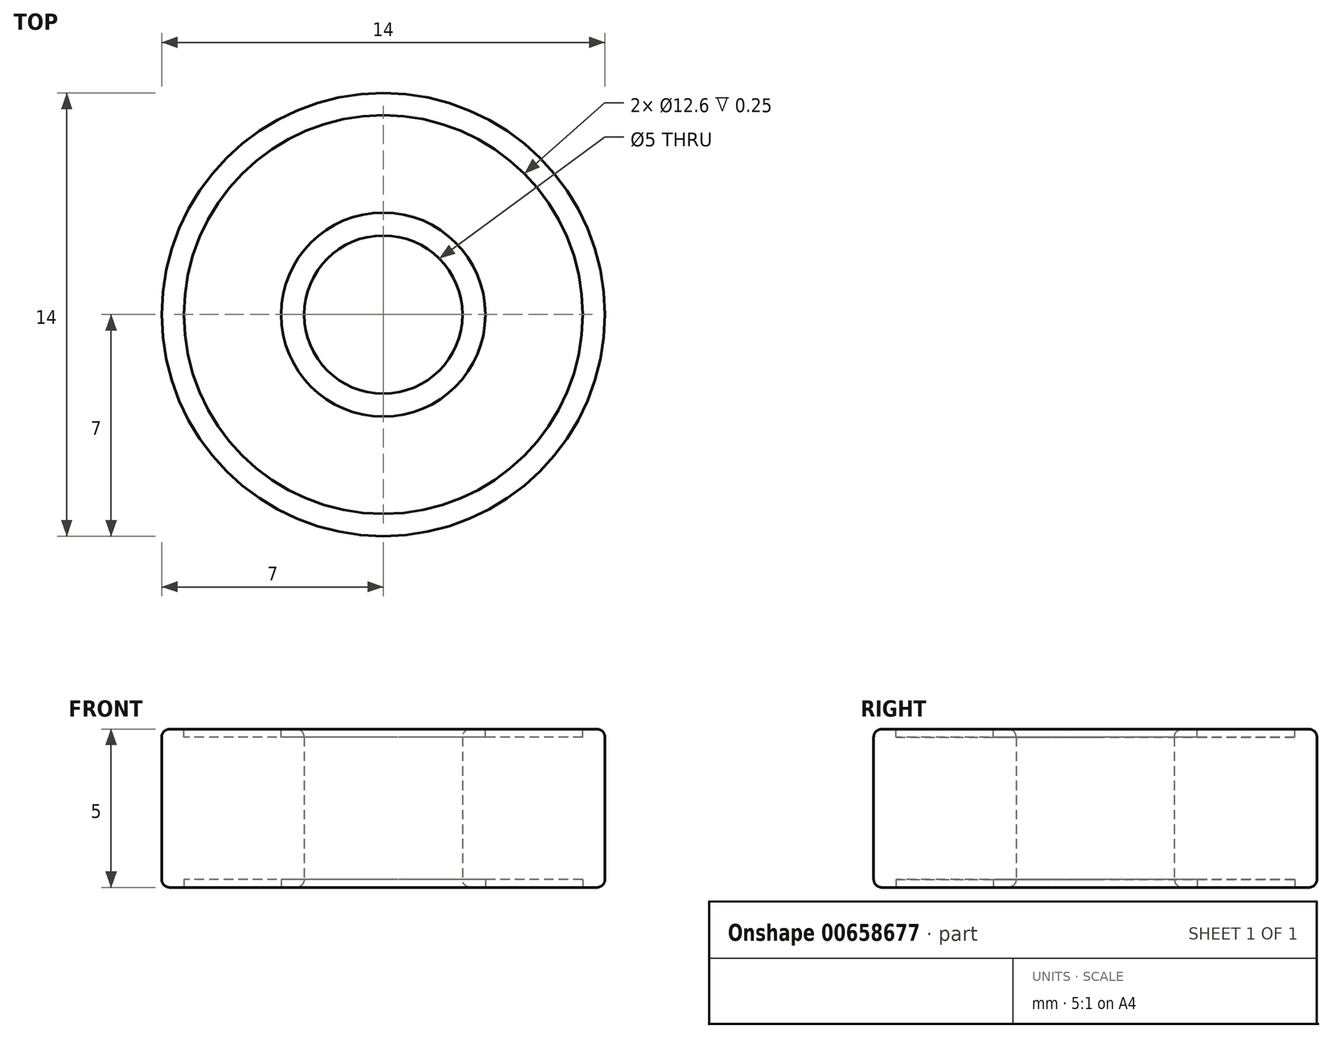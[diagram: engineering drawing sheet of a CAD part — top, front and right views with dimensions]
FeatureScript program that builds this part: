
annotation { "Feature Type Name" : "Feature", "Feature Type Description" : "" }
export const myFeature = defineFeature(function(context is Context, id is Id, definition is map)
    precondition{}
    {
        {
            var Q0;
            Q0=qCreatedBy(makeId("Top.planeOp"),FACE);
            var sketch = newSketch(context, id + "F0", { "sketchPlane" : qUnion([Q0])});
            skCircle(sketch, "E0", {"center": v(0, 0) * mm, "radius": 7 * mm});
            skCircle(sketch, "E1", {"center": v(0, 0) * mm, "radius": 2.5 * mm});
            skSolve(sketch);
        }
        {
            var Q0;
            Q0=makeQuery(id+"F0.imprint","IMPRINT",FACE,{"disambiguationData":[TD([[makeQuery(id+"F0.imprint","IMPRINT",EDGE,{"derivedFrom":sQuery(id+"F0.wireOp",EDGE,"E0")}),1.0]])]});
            extrude(context, id + "F1", {"entities" : qUnion([Q0]), "depth" : 2.5 * mm});
        }
        {
            var Q0;
            Q0=makeQuery(id+"F1.opExtrude","CAP_FACE",FACE,{"disambiguationData":[OSD([sQuery(id+"F0.wireOp",EDGE,"E0"),sQuery(id+"F0.wireOp",EDGE,"E1")])],"isStart":false});
            var sketch = newSketch(context, id + "F2", { "sketchPlane" : qUnion([Q0])});
            skCircle(sketch, "E2", {"center": v(0, 0) * mm, "radius": 3.22 * mm});
            skCircle(sketch, "E3", {"center": v(0, 0) * mm, "radius": 6.3 * mm});
            skSolve(sketch);
        }
        {
            var Q0;
            Q0=makeQuery(id+"F2.imprint","IMPRINT",FACE,{"disambiguationData":[TD([[makeQuery(id+"F2.imprint","IMPRINT",EDGE,{"derivedFrom":sQuery(id+"F2.wireOp",EDGE,"E2")}),-1.0]])]});
            extrude(context, id + "F3", {"entities" : qUnion([Q0]), "operationType" : NewBodyOperationType.REMOVE, "oppositeDirection" : true, "depth" : .25 * mm});
        }
        {
            var Q0;
            Q0=makeQuery(id+"F1.opExtrude","CAP_EDGE",EDGE,{"disambiguationData":[OSD([sQuery(id+"F0.wireOp",EDGE,"E0")])],"isStart":false});
            var Q1;
            Q1=makeQuery(id+"F1.opExtrude","CAP_EDGE",EDGE,{"disambiguationData":[OSD([sQuery(id+"F0.wireOp",EDGE,"E1")])],"isStart":false});
            fillet(context, id + "F4", {"entities" : qUnion([Q0, Q1]), "radius" : .25 * mm, "tangentPropagation" : true, "allowEdgeOverflow" : false});
        }
        {
            var Q0;
            Q0=makeQuery(id+"F1.opExtrude","SWEPT_BODY",BODY,{"disambiguationData":[OSD([sQuery(id+"F0.wireOp",EDGE,"E0"),sQuery(id+"F0.wireOp",EDGE,"E1")])]});
            var Q1;
            Q1=makeQuery(id+"F1.opExtrude","CAP_FACE",FACE,{"disambiguationData":[OSD([sQuery(id+"F0.wireOp",EDGE,"E0"),sQuery(id+"F0.wireOp",EDGE,"E1")])],"isStart":true});
            mirror(context, id + "F5", {"operationType" : NewBodyOperationType.ADD, "entities" : qUnion([Q0]), "mirrorPlane" : qUnion([Q1])});
        }
    });
